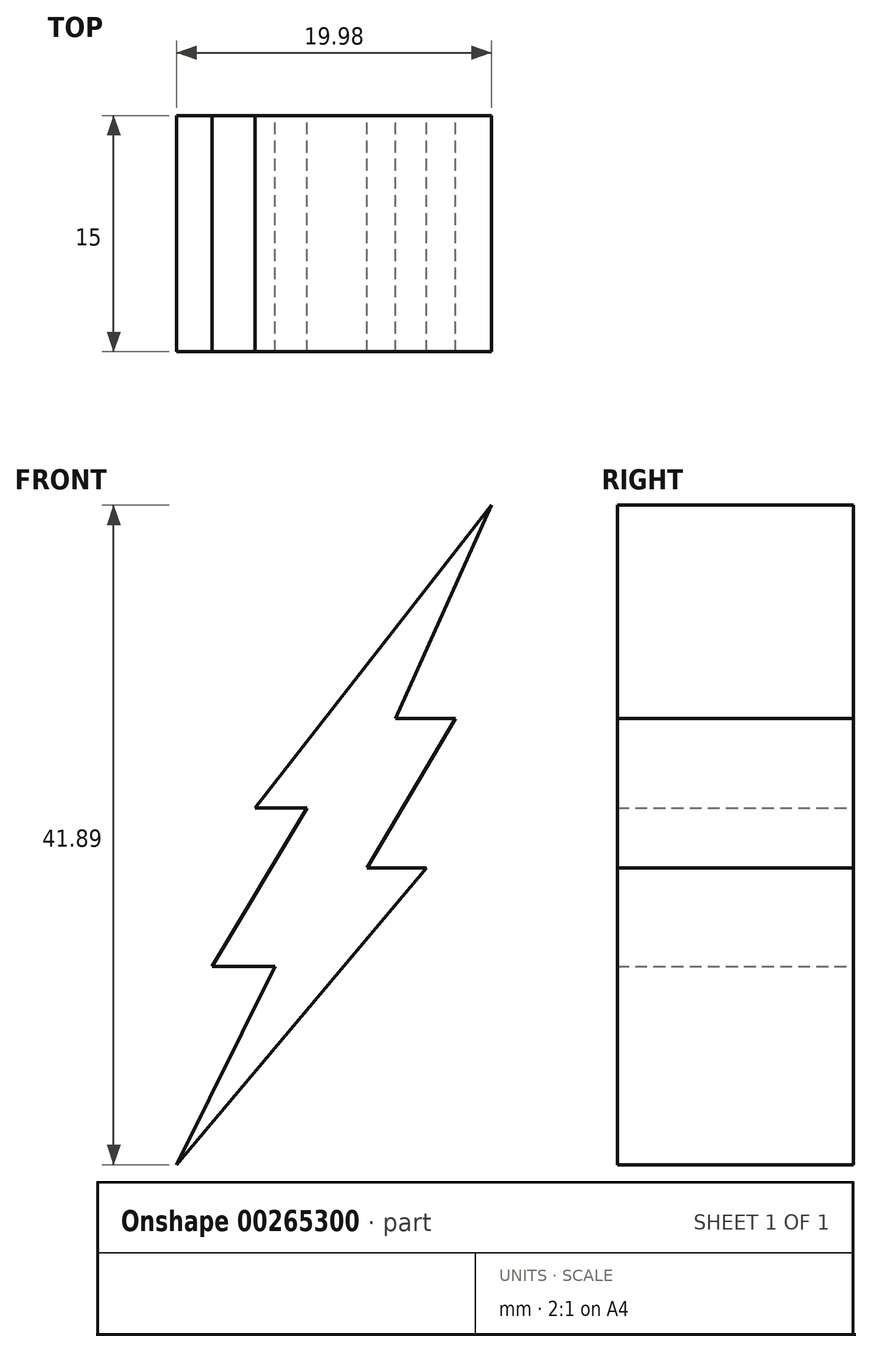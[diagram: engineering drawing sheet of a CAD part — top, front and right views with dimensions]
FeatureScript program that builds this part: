
annotation { "Feature Type Name" : "Feature", "Feature Type Description" : "" }
export const myFeature = defineFeature(function(context is Context, id is Id, definition is map)
    precondition{}
    {
        {
            var Q0;
            Q0=qCreatedBy(makeId("Front.planeOp"),FACE);
            var sketch = newSketch(context, id + "F0", { "sketchPlane" : qUnion([Q0])});
            skArc(sketch, "E0", {"start": v(-28.54, 58.3) * mm, "mid": v(-46.42, 49.8) * mm, "end": v(-39.07, 31.42) * mm});
            skPoint(sketch, "E0.first.point", {"position": v(-30.01, 58.68) * mm});
            skPoint(sketch, "E0.second.point", {"position": v(-25.94, 31.87) * mm});
            skPoint(sketch, "E0.third.point", {"position": v(-45.62, 37.54) * mm});
            skLineSegment(sketch, "E1", {"start": v(-23.02, 65.36) * mm, "end": v(-38.04, 46.14) * mm});
            skLineSegment(sketch, "E2", {"start": v(-38.04, 46.14) * mm, "end": v(-34.73, 46.14) * mm});
            skLineSegment(sketch, "E3", {"start": v(-34.73, 46.14) * mm, "end": v(-40.76, 36.08) * mm});
            skLineSegment(sketch, "E4", {"start": v(-40.76, 36.08) * mm, "end": v(-36.76, 36.08) * mm});
            skLineSegment(sketch, "E5", {"start": v(-36.76, 36.08) * mm, "end": v(-43, 23.47) * mm});
            skLineSegment(sketch, "E6", {"start": v(-43, 23.47) * mm, "end": v(-27.15, 42.32) * mm});
            skLineSegment(sketch, "E7", {"start": v(-27.15, 42.32) * mm, "end": v(-30.9, 42.32) * mm});
            skLineSegment(sketch, "E8", {"start": v(-30.9, 42.32) * mm, "end": v(-25.3, 51.8) * mm});
            skLineSegment(sketch, "E9", {"start": v(-25.3, 51.8) * mm, "end": v(-29.12, 51.8) * mm});
            skLineSegment(sketch, "E10", {"start": v(-29.12, 51.8) * mm, "end": v(-23.02, 65.36) * mm});
            skArc(sketch, "E11.trimOffspring", {"start": v(-36.98, 30.63) * mm, "mid": v(-19.47, 39.3) * mm, "end": v(-26.56, 57.5) * mm});
            skSolve(sketch);
        }
        {
            var Q0;
            {var subQ13=sQuery(id+"F0.wireOp",EDGE,"E2");Q0=makeQuery(id+"F0.imprint","IMPRINT",FACE,{"disambiguationData":[TD([[makeQuery(id+"F0.imprint","IMPRINT",EDGE,{"derivedFrom":subQ13}),1.0]])]});}
            extrude(context, id + "F1", {"entities" : qUnion([Q0]), "offsetDistance" : 25 * mm, "depth" : 15 * mm});
        }
    });
